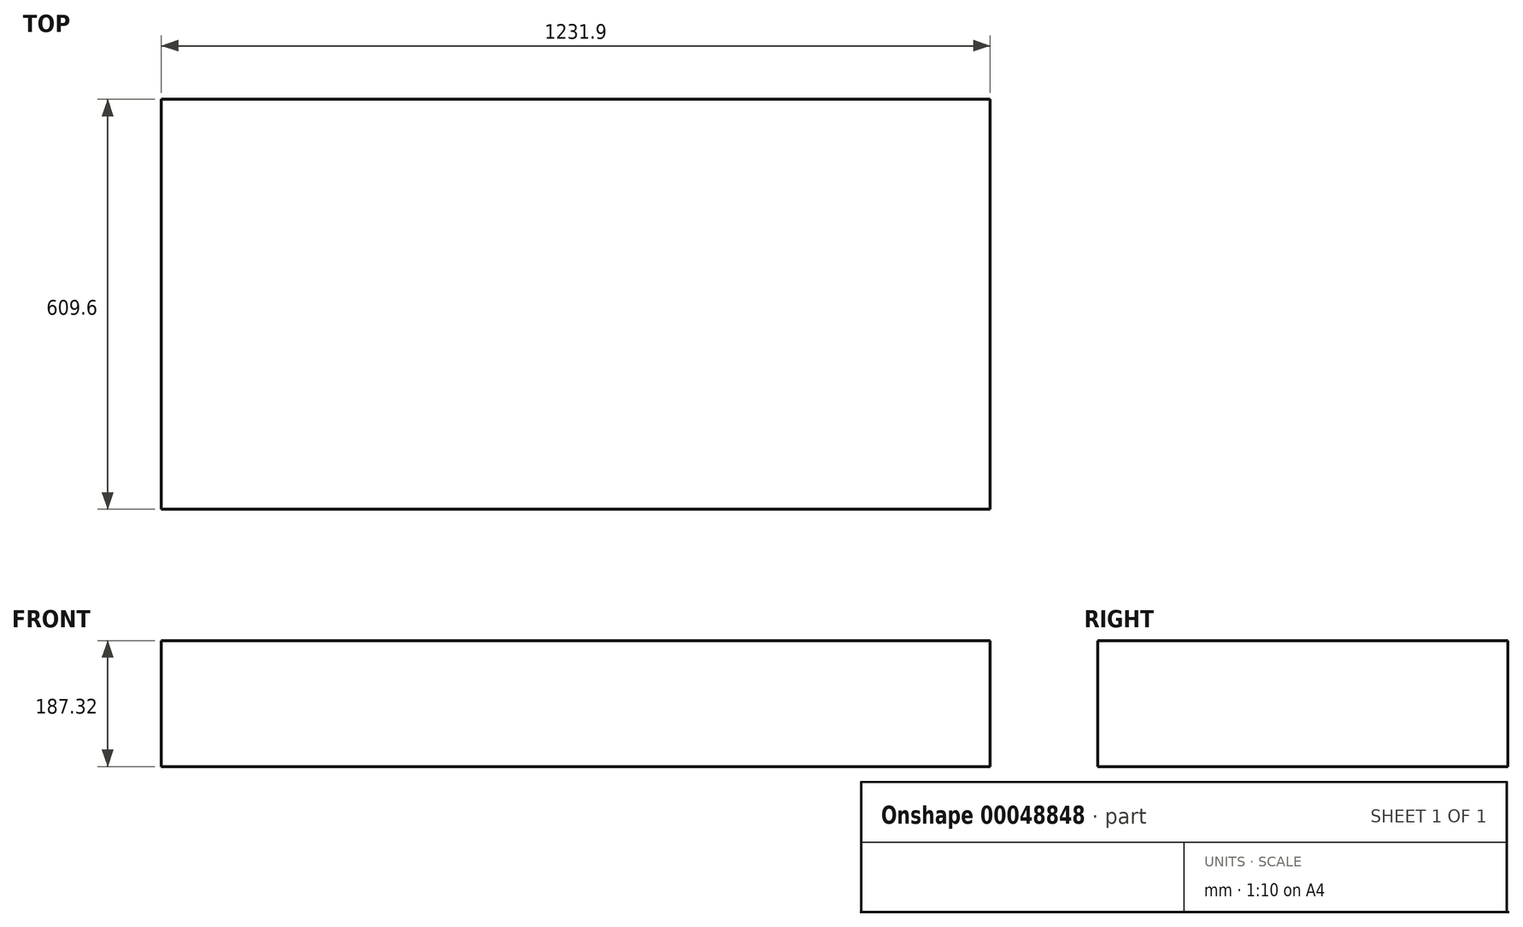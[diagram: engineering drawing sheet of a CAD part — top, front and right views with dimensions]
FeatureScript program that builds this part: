
annotation { "Feature Type Name" : "Feature", "Feature Type Description" : "" }
export const myFeature = defineFeature(function(context is Context, id is Id, definition is map)
    precondition{}
    {
        {
            var Q0;
            Q0=qCreatedBy(makeId("Top.planeOp"),FACE);
            var sketch = newSketch(context, id + "F0", { "sketchPlane" : qUnion([Q0])});
            skLineSegment(sketch, "E0.rect.bottom", {"start": v(615.95, -304.8) * mm, "end": v(-615.95, -304.8) * mm});
            skLineSegment(sketch, "E0.rect.top", {"start": v(615.95, 304.8) * mm, "end": v(-615.95, 304.8) * mm});
            skLineSegment(sketch, "E0.rect.left", {"start": v(615.95, -304.8) * mm, "end": v(615.95, 304.8) * mm});
            skLineSegment(sketch, "E0.rect.right", {"start": v(-615.95, -304.8) * mm, "end": v(-615.95, 304.8) * mm});
            skPoint(sketch, "E0.rect.middle", {"position": v(0, 0) * mm});
            skSolve(sketch);
        }
        {
            var Q0;
            Q0=makeQuery(id+"F0.imprint","IMPRINT",FACE,{"disambiguationData":[TD([[makeQuery(id+"F0.imprint","IMPRINT",EDGE,{"derivedFrom":sQuery(id+"F0.wireOp",EDGE,"E0.rect.bottom")}),-1.0]])]});
            extrude(context, id + "F1", {"entities" : qUnion([Q0]), "depth" : 187.32 * mm});
        }
    });
